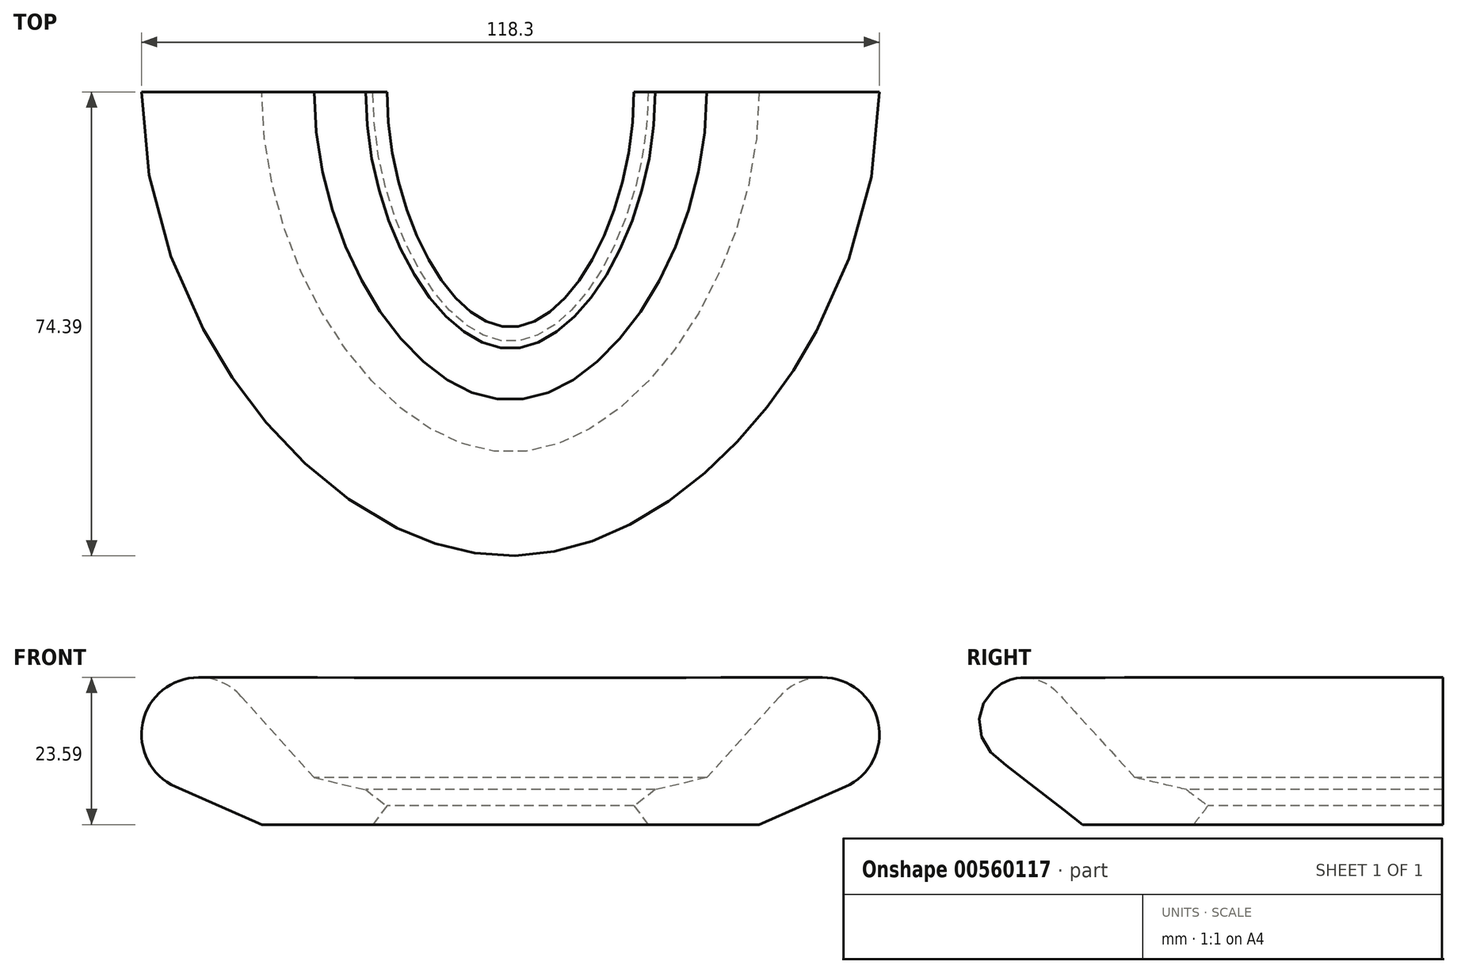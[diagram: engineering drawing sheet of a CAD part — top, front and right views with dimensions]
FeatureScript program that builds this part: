
annotation { "Feature Type Name" : "Feature", "Feature Type Description" : "" }
export const myFeature = defineFeature(function(context is Context, id is Id, definition is map)
    precondition{}
    {
        {
            var Q0;
            Q0=qCreatedBy(makeId("Front.planeOp"),FACE);
            var sketch = newSketch(context, id + "F0", { "sketchPlane" : qUnion([Q0])});
            skArc(sketch, "E0", {"start": v(-43.19, 20.55) * mm, "mid": v(-57.42, 19.8) * mm, "end": v(-53.68, 6.06) * mm});
            skLineSegment(sketch, "E1", {"start": v(-22.09, 0) * mm, "end": v(-39.87, 0) * mm});
            skLineSegment(sketch, "E2", {"start": v(-39.87, 0) * mm, "end": v(-53.68, 6.06) * mm});
            skLineSegment(sketch, "E3", {"start": v(-43.19, 20.55) * mm, "end": v(-31.5, 7.52) * mm});
            skLineSegment(sketch, "E4", {"start": v(-31.5, 7.52) * mm, "end": v(-23.23, 5.6) * mm});
            skLineSegment(sketch, "E5", {"start": v(-23.23, 5.6) * mm, "end": v(-19.8, 3) * mm});
            skLineSegment(sketch, "E6", {"start": v(-19.8, 3) * mm, "end": v(-22.09, 0) * mm});
            skLineSegment(sketch, "E7.MirrorCS", {"start": v(19.8, 3) * mm, "end": v(22.09, 0) * mm});
            skLineSegment(sketch, "E8.MirrorCS", {"start": v(23.23, 5.6) * mm, "end": v(19.8, 3) * mm});
            skLineSegment(sketch, "E9.MirrorCS", {"start": v(31.5, 7.52) * mm, "end": v(23.23, 5.6) * mm});
            skLineSegment(sketch, "E10.MirrorCS", {"start": v(43.19, 20.55) * mm, "end": v(31.5, 7.52) * mm});
            skLineSegment(sketch, "E11.MirrorCS", {"start": v(22.09, 0) * mm, "end": v(39.87, 0) * mm});
            skLineSegment(sketch, "E12.MirrorCS", {"start": v(39.87, 0) * mm, "end": v(53.68, 6.06) * mm});
            skArc(sketch, "E13.MirrorCS", {"start": v(43.19, 20.55) * mm, "mid": v(57.42, 19.8) * mm, "end": v(53.68, 6.06) * mm});
            skSolve(sketch);
        }
        {
            var Q0;
            Q0=qCreatedBy(makeId("Right.planeOp"),FACE);
            var sketch = newSketch(context, id + "F1", { "sketchPlane" : qUnion([Q0])});
            skArc(sketch, "E14", {"start": v(-61.88, 21.2) * mm, "mid": v(-72.48, 21.23) * mm, "end": v(-71.6, 10.66) * mm});
            skLineSegment(sketch, "E15", {"start": v(-40, 0) * mm, "end": v(-57.79, 0) * mm});
            skLineSegment(sketch, "E16", {"start": v(-57.79, 0) * mm, "end": v(-71.6, 10.66) * mm});
            skLineSegment(sketch, "E17", {"start": v(-61.88, 21.2) * mm, "end": v(-49.4, 7.52) * mm});
            skLineSegment(sketch, "E18", {"start": v(-49.4, 7.52) * mm, "end": v(-41.15, 5.6) * mm});
            skLineSegment(sketch, "E19", {"start": v(-41.15, 5.6) * mm, "end": v(-37.72, 3) * mm});
            skLineSegment(sketch, "E20", {"start": v(-40, 0) * mm, "end": v(-37.72, 3) * mm});
            skSolve(sketch);
        }
        {
            var Q0;
            Q0=makeQuery(id+"F0.imprint","IMPRINT",FACE,{"disambiguationData":[TD([[makeQuery(id+"F0.imprint","IMPRINT",EDGE,{"derivedFrom":sQuery(id+"F0.wireOp",EDGE,"E7.MirrorCS")}),1.0]])]});
            var Q1;
            Q1=makeQuery(id+"F1.imprint","IMPRINT",FACE,{"disambiguationData":[TD([[makeQuery(id+"F1.imprint","IMPRINT",EDGE,{"derivedFrom":sQuery(id+"F1.wireOp",EDGE,"E14")}),1.0]])]});
            var Q2;
            Q2=makeQuery(id+"F0.imprint","IMPRINT",FACE,{"disambiguationData":[TD([[makeQuery(id+"F0.imprint","IMPRINT",EDGE,{"derivedFrom":sQuery(id+"F0.wireOp",EDGE,"E0")}),1.0]])]});
            loft(context, id + "F2", {"startCondition" : LoftEndDerivativeType.NORMAL_TO_PROFILE, "startMagnitude" : 1, "endCondition" : LoftEndDerivativeType.NORMAL_TO_PROFILE, "endMagnitude" : 1, "sheetProfilesArray" : [{ "sheetProfileEntities" : qUnion([Q0]) }, { "sheetProfileEntities" : qUnion([Q1]) }, { "sheetProfileEntities" : qUnion([Q2]) }]});
        }
    });
